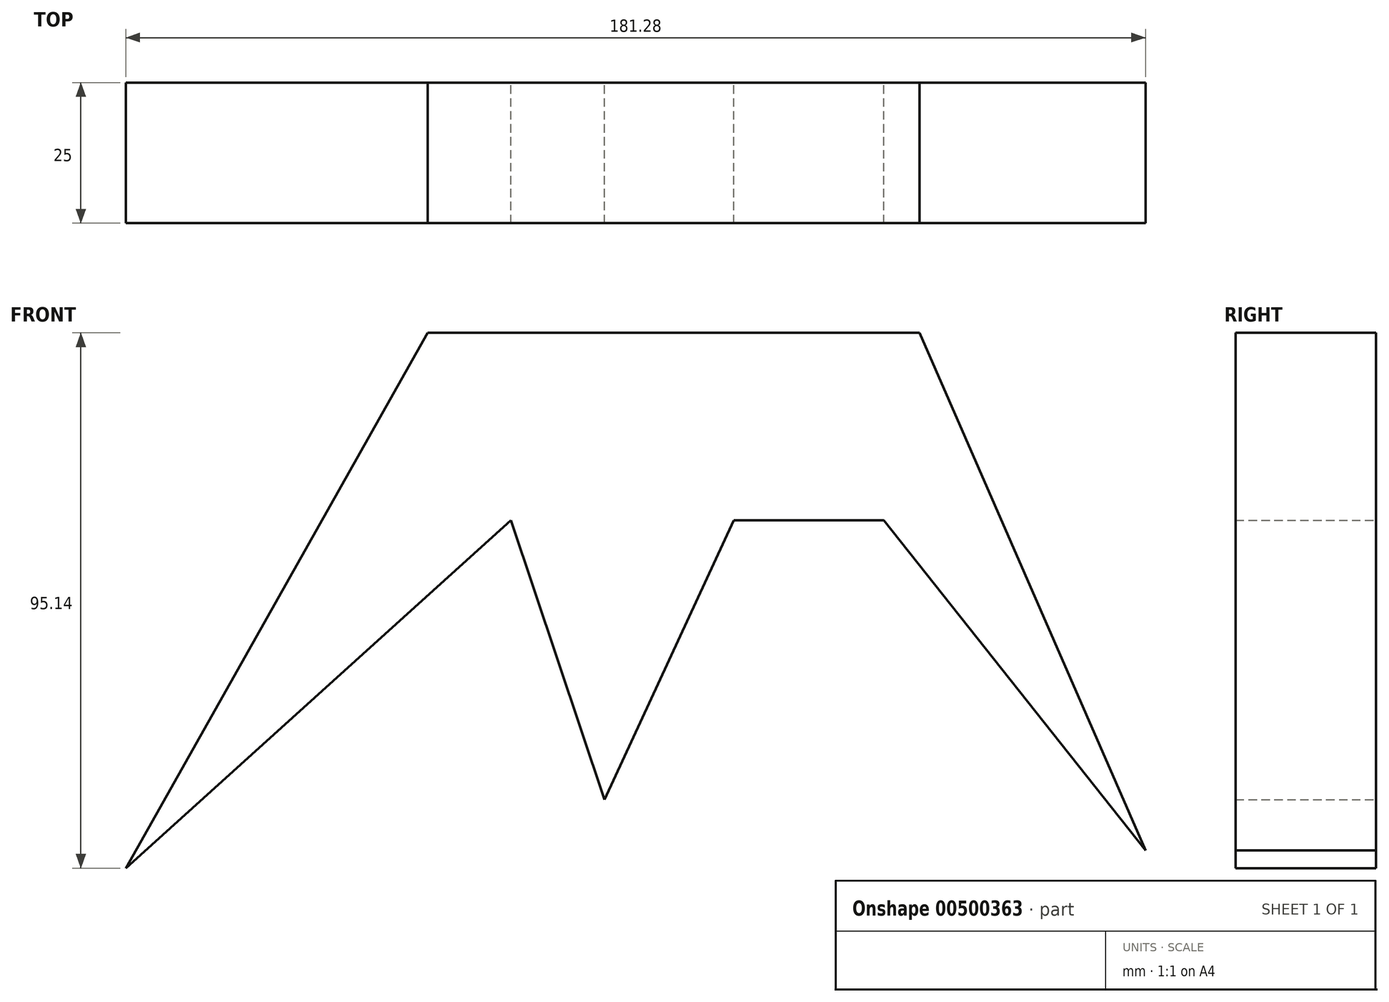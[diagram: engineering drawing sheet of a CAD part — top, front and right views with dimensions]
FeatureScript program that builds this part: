
annotation { "Feature Type Name" : "Feature", "Feature Type Description" : "" }
export const myFeature = defineFeature(function(context is Context, id is Id, definition is map)
    precondition{}
    {
        {
            var Q0;
            Q0=qCreatedBy(makeId("Front.planeOp"),FACE);
            var sketch = newSketch(context, id + "F0", { "sketchPlane" : qUnion([Q0])});
            skLineSegment(sketch, "E0", {"start": v(-31.45, 65.54) * mm, "end": v(-85.1, -29.6) * mm});
            skLineSegment(sketch, "E1", {"start": v(-31.45, 65.54) * mm, "end": v(56.02, 65.54) * mm});
            skLineSegment(sketch, "E2", {"start": v(56.02, 65.54) * mm, "end": v(96.2, -26.43) * mm});
            skLineSegment(sketch, "E3", {"start": v(-85.1, -29.6) * mm, "end": v(-16.65, 32.24) * mm});
            skLineSegment(sketch, "E4", {"start": v(-16.65, 32.24) * mm, "end": v(0, -17.44) * mm});
            skLineSegment(sketch, "E5", {"start": v(0, -17.44) * mm, "end": v(23, 32.24) * mm});
            skLineSegment(sketch, "E6", {"start": v(23, 32.24) * mm, "end": v(49.68, 32.24) * mm});
            skLineSegment(sketch, "E7", {"start": v(49.42, 32.5) * mm, "end": v(96.2, -26.43) * mm});
            skSolve(sketch);
        }
        {
            var Q0;
            Q0=makeQuery(id+"F0.imprint","IMPRINT",FACE,{"disambiguationData":[TD([[makeQuery(id+"F0.imprint","IMPRINT",EDGE,{"derivedFrom":sQuery(id+"F0.wireOp",EDGE,"E0")}),1.0]])]});
            extrude(context, id + "F1", {"entities" : qUnion([Q0]), "depth" : 25 * mm});
        }
    });
